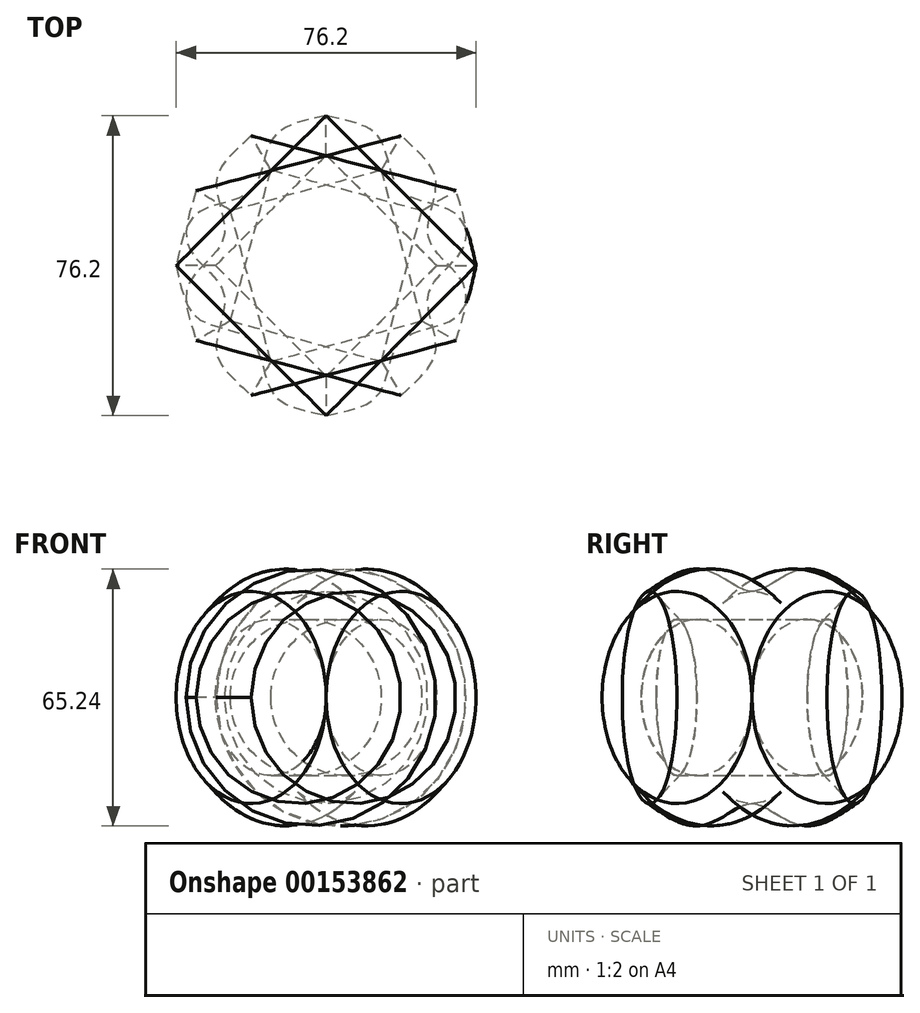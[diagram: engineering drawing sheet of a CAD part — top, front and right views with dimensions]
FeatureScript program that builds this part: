
annotation { "Feature Type Name" : "Feature", "Feature Type Description" : "" }
export const myFeature = defineFeature(function(context is Context, id is Id, definition is map)
    precondition{}
    {
        {
            var Q0;
            Q0=qCreatedBy(makeId("Top.planeOp"),FACE);
            var sketch = newSketch(context, id + "F0", { "sketchPlane" : qUnion([Q0])});
            skLineSegment(sketch, "E0", {"start": v(0, -38.1) * mm, "end": v(0, 0) * mm, "construction": true});
            skLineSegment(sketch, "E1", {"start": v(0, 0) * mm, "end": v(-38.1, 0) * mm, "construction": true});
            skLineSegment(sketch, "E2", {"start": v(-38.1, 0) * mm, "end": v(0, -38.1) * mm, "construction": true});
            skLineSegment(sketch, "E3", {"start": v(0, 0) * mm, "end": v(-26.94, -26.94) * mm, "construction": true});
            skLineSegment(sketch, "E4", {"start": v(-38.1, 0) * mm, "end": v(-26.94, -26.94) * mm, "construction": true});
            skLineSegment(sketch, "E5", {"start": v(0, 0) * mm, "end": v(-35.2, -14.58) * mm, "construction": true});
            skLineSegment(sketch, "E6", {"start": v(-26.94, -26.94) * mm, "end": v(0, -38.1) * mm, "construction": true});
            skLineSegment(sketch, "E7", {"start": v(0, 0) * mm, "end": v(-14.58, -35.2) * mm, "construction": true});
            skFitSpline(sketch, "E8", {"points": [v(-38.1, 0) * mm, v(-32.52, -13.47) * mm, v(-19.05, -19.05) * mm, v(-13.47, -32.52) * mm, v(0, -38.1) * mm], "startDerivative": vector(15.94, -65) * mm, "endDerivative": vector(65, -15.94) * mm});
            skPoint(sketch, "E9.center", {"position": v(-7.3, 13.46) * mm});
            skPoint(sketch, "E10.center", {"position": v(0, 0) * mm});
            skLineSegment(sketch, "E11", {"start": v(-38.1, 0) * mm, "end": v(-28.09, 0) * mm});
            skLineSegment(sketch, "E12", {"start": v(-28.09, 0) * mm, "end": v(0, -28.09) * mm});
            skLineSegment(sketch, "E13", {"start": v(0, -28.09) * mm, "end": v(0, -38.1) * mm});
            skLineSegment(sketch, "E14", {"start": v(0, 0) * mm, "end": v(16.1, -16.1) * mm, "construction": true});
            skSolve(sketch);
        }
        {
            var Q0;
            Q0 = qSketchRegion(id + "F0", true);
            var Q1;
            Q1=sQuery(id+"F0.wireOp",EDGE,"E14");
            revolve(context, id + "F1", {"entities" : qUnion([Q0]), "axis" : qUnion([Q1]), "revolveType" : RevolveType.FULL});
        }
        {
            var Q0;
            Q0=qCreatedBy(makeId("Front.planeOp"),FACE);
            var sketch = newSketch(context, id + "F2", { "sketchPlane" : qUnion([Q0])});
            skLineSegment(sketch, "E15", {"start": v(0, 72.88) * mm, "end": v(0, -57.43) * mm, "construction": true});
            skSolve(sketch);
        }
        {
            var Q0;
            Q0=makeQuery(id+"F1.opRevolve","SWEPT_BODY",BODY,{"disambiguationData":[OSD([sQuery(id+"F0.wireOp",EDGE,"E8"),sQuery(id+"F0.wireOp",EDGE,"E11"),sQuery(id+"F0.wireOp",EDGE,"E12"),sQuery(id+"F0.wireOp",EDGE,"E13")])]});
            var Q1;
            Q1=sQuery(id+"F2.wireOp",EDGE,"E15");
            circularPattern(context, id + "F3", {"entities" : qUnion([Q0]), "axis" : qUnion([Q1]), "angle" : 30 * degree, "instanceCount" : 4});
        }
    });
